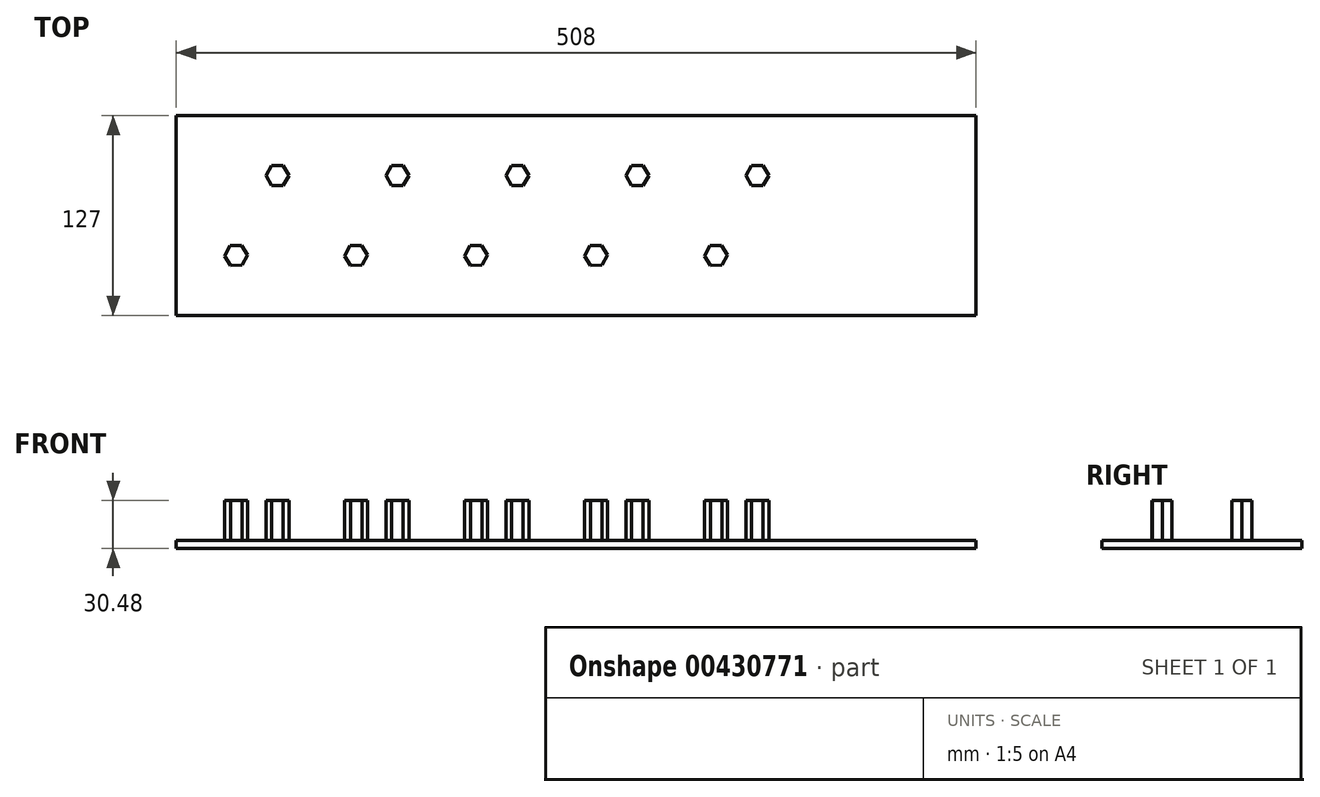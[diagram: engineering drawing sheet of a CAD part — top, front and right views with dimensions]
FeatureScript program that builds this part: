
annotation { "Feature Type Name" : "Feature", "Feature Type Description" : "" }
export const myFeature = defineFeature(function(context is Context, id is Id, definition is map)
    precondition{}
    {
        {
            var Q0;
            Q0=qCreatedBy(makeId("Top.planeOp"),FACE);
            var sketch = newSketch(context, id + "F0", { "sketchPlane" : qUnion([Q0])});
            skLineSegment(sketch, "E0.bottom", {"start": v(0, 0) * mm, "end": v(508, 0) * mm});
            skLineSegment(sketch, "E0.top", {"start": v(0, 127) * mm, "end": v(508, 127) * mm});
            skLineSegment(sketch, "E0.left", {"start": v(0, 0) * mm, "end": v(0, 127) * mm});
            skLineSegment(sketch, "E0.right", {"start": v(508, 0) * mm, "end": v(508, 127) * mm});
            skSolve(sketch);
        }
        {
            var Q0;
            Q0=makeQuery(id+"F0.imprint","IMPRINT",FACE,{"disambiguationData":[TD([[makeQuery(id+"F0.imprint","IMPRINT",EDGE,{"derivedFrom":sQuery(id+"F0.wireOp",EDGE,"E0.bottom")}),1.0]])]});
            extrude(context, id + "F1", {"entities" : qUnion([Q0]), "depth" : 5.08 * mm});
        }
        {
            var Q0;
            Q0=makeQuery(id+"F1.opExtrude","CAP_FACE",FACE,{"disambiguationData":[OSD([sQuery(id+"F0.wireOp",EDGE,"E0.bottom"),sQuery(id+"F0.wireOp",EDGE,"E0.top"),sQuery(id+"F0.wireOp",EDGE,"E0.left"),sQuery(id+"F0.wireOp",EDGE,"E0.right")])],"isStart":false});
            var sketch = newSketch(context, id + "F2", { "sketchPlane" : qUnion([Q0])});
            skCircle(sketch, "E1.cCircle", {"center": v(38.1, 38.1) * mm, "radius": 6.29 * mm, "construction": true});
            skLineSegment(sketch, "E1.0", {"start": v(41.55, 44.49) * mm, "end": v(45.36, 38.3) * mm});
            skLineSegment(sketch, "E1.1", {"start": v(45.36, 38.3) * mm, "end": v(41.9, 31.92) * mm});
            skLineSegment(sketch, "E1.2", {"start": v(41.9, 31.92) * mm, "end": v(34.65, 31.71) * mm});
            skLineSegment(sketch, "E1.3", {"start": v(34.65, 31.71) * mm, "end": v(30.84, 37.9) * mm});
            skLineSegment(sketch, "E1.4", {"start": v(30.84, 37.9) * mm, "end": v(34.3, 44.28) * mm});
            skLineSegment(sketch, "E1.5", {"start": v(34.3, 44.28) * mm, "end": v(41.55, 44.49) * mm});
            skPoint(sketch, "E1.0.midPoint", {"position": v(43.45, 41.4) * mm});
            skCircle(sketch, "E2.cCircle", {"center": v(64.28, 88.9) * mm, "radius": 6.29 * mm, "construction": true});
            skLineSegment(sketch, "E2.0", {"start": v(71.54, 88.9) * mm, "end": v(67.9, 82.6) * mm});
            skLineSegment(sketch, "E2.1", {"start": v(67.9, 82.6) * mm, "end": v(60.64, 82.62) * mm});
            skLineSegment(sketch, "E2.2", {"start": v(60.64, 82.62) * mm, "end": v(57.02, 88.9) * mm});
            skLineSegment(sketch, "E2.3", {"start": v(57.02, 88.9) * mm, "end": v(60.66, 95.2) * mm});
            skLineSegment(sketch, "E2.4", {"start": v(60.66, 95.2) * mm, "end": v(67.92, 95.18) * mm});
            skLineSegment(sketch, "E2.5", {"start": v(67.92, 95.18) * mm, "end": v(71.54, 88.9) * mm});
            skPoint(sketch, "E2.0.midPoint", {"position": v(69.72, 85.75) * mm});
            skLineSegment(sketch, "E3.1.0.0", {"start": v(136.86, 95.2) * mm, "end": v(144.12, 95.18) * mm});
            skLineSegment(sketch, "E3.1.0.1", {"start": v(133.22, 88.9) * mm, "end": v(136.86, 95.2) * mm});
            skLineSegment(sketch, "E3.1.0.2", {"start": v(136.84, 82.62) * mm, "end": v(133.22, 88.9) * mm});
            skLineSegment(sketch, "E3.1.0.3", {"start": v(144.1, 82.6) * mm, "end": v(136.84, 82.62) * mm});
            skLineSegment(sketch, "E3.1.0.4", {"start": v(147.74, 88.9) * mm, "end": v(144.1, 82.6) * mm});
            skLineSegment(sketch, "E3.1.0.5", {"start": v(144.12, 95.18) * mm, "end": v(147.74, 88.9) * mm});
            skLineSegment(sketch, "E3.1.0.6", {"start": v(118.1, 31.92) * mm, "end": v(110.85, 31.71) * mm});
            skLineSegment(sketch, "E3.1.0.7", {"start": v(121.56, 38.3) * mm, "end": v(118.1, 31.92) * mm});
            skLineSegment(sketch, "E3.1.0.8", {"start": v(117.75, 44.49) * mm, "end": v(121.56, 38.3) * mm});
            skLineSegment(sketch, "E3.1.0.9", {"start": v(110.5, 44.28) * mm, "end": v(117.75, 44.49) * mm});
            skLineSegment(sketch, "E3.1.0.10", {"start": v(107.04, 37.9) * mm, "end": v(110.5, 44.28) * mm});
            skLineSegment(sketch, "E3.1.0.11", {"start": v(110.85, 31.71) * mm, "end": v(107.04, 37.9) * mm});
            skLineSegment(sketch, "E3.2.0.0", {"start": v(213.06, 95.2) * mm, "end": v(220.32, 95.18) * mm});
            skLineSegment(sketch, "E3.2.0.1", {"start": v(209.42, 88.9) * mm, "end": v(213.06, 95.2) * mm});
            skLineSegment(sketch, "E3.2.0.2", {"start": v(213.04, 82.62) * mm, "end": v(209.42, 88.9) * mm});
            skLineSegment(sketch, "E3.2.0.3", {"start": v(220.3, 82.6) * mm, "end": v(213.04, 82.62) * mm});
            skLineSegment(sketch, "E3.2.0.4", {"start": v(223.94, 88.9) * mm, "end": v(220.3, 82.6) * mm});
            skLineSegment(sketch, "E3.2.0.5", {"start": v(220.32, 95.18) * mm, "end": v(223.94, 88.9) * mm});
            skLineSegment(sketch, "E3.2.0.6", {"start": v(194.3, 31.92) * mm, "end": v(187.05, 31.71) * mm});
            skLineSegment(sketch, "E3.2.0.7", {"start": v(197.76, 38.3) * mm, "end": v(194.3, 31.92) * mm});
            skLineSegment(sketch, "E3.2.0.8", {"start": v(193.95, 44.49) * mm, "end": v(197.76, 38.3) * mm});
            skLineSegment(sketch, "E3.2.0.9", {"start": v(186.7, 44.28) * mm, "end": v(193.95, 44.49) * mm});
            skLineSegment(sketch, "E3.2.0.10", {"start": v(183.24, 37.9) * mm, "end": v(186.7, 44.28) * mm});
            skLineSegment(sketch, "E3.2.0.11", {"start": v(187.05, 31.71) * mm, "end": v(183.24, 37.9) * mm});
            skLineSegment(sketch, "E3.3.0.0", {"start": v(289.26, 95.2) * mm, "end": v(296.52, 95.18) * mm});
            skLineSegment(sketch, "E3.3.0.1", {"start": v(285.62, 88.9) * mm, "end": v(289.26, 95.2) * mm});
            skLineSegment(sketch, "E3.3.0.2", {"start": v(289.24, 82.62) * mm, "end": v(285.62, 88.9) * mm});
            skLineSegment(sketch, "E3.3.0.3", {"start": v(296.5, 82.6) * mm, "end": v(289.24, 82.62) * mm});
            skLineSegment(sketch, "E3.3.0.4", {"start": v(300.14, 88.9) * mm, "end": v(296.5, 82.6) * mm});
            skLineSegment(sketch, "E3.3.0.5", {"start": v(296.52, 95.18) * mm, "end": v(300.14, 88.9) * mm});
            skLineSegment(sketch, "E3.3.0.6", {"start": v(270.5, 31.92) * mm, "end": v(263.25, 31.71) * mm});
            skLineSegment(sketch, "E3.3.0.7", {"start": v(273.96, 38.3) * mm, "end": v(270.5, 31.92) * mm});
            skLineSegment(sketch, "E3.3.0.8", {"start": v(270.15, 44.49) * mm, "end": v(273.96, 38.3) * mm});
            skLineSegment(sketch, "E3.3.0.9", {"start": v(262.9, 44.28) * mm, "end": v(270.15, 44.49) * mm});
            skLineSegment(sketch, "E3.3.0.10", {"start": v(259.44, 37.9) * mm, "end": v(262.9, 44.28) * mm});
            skLineSegment(sketch, "E3.3.0.11", {"start": v(263.25, 31.71) * mm, "end": v(259.44, 37.9) * mm});
            skLineSegment(sketch, "E3.4.0.0", {"start": v(365.46, 95.2) * mm, "end": v(372.72, 95.18) * mm});
            skLineSegment(sketch, "E3.4.0.1", {"start": v(361.82, 88.9) * mm, "end": v(365.46, 95.2) * mm});
            skLineSegment(sketch, "E3.4.0.2", {"start": v(365.44, 82.62) * mm, "end": v(361.82, 88.9) * mm});
            skLineSegment(sketch, "E3.4.0.3", {"start": v(372.7, 82.6) * mm, "end": v(365.44, 82.62) * mm});
            skLineSegment(sketch, "E3.4.0.4", {"start": v(376.34, 88.9) * mm, "end": v(372.7, 82.6) * mm});
            skLineSegment(sketch, "E3.4.0.5", {"start": v(372.72, 95.18) * mm, "end": v(376.34, 88.9) * mm});
            skLineSegment(sketch, "E3.4.0.6", {"start": v(346.7, 31.92) * mm, "end": v(339.45, 31.71) * mm});
            skLineSegment(sketch, "E3.4.0.7", {"start": v(350.16, 38.3) * mm, "end": v(346.7, 31.92) * mm});
            skLineSegment(sketch, "E3.4.0.8", {"start": v(346.35, 44.49) * mm, "end": v(350.16, 38.3) * mm});
            skLineSegment(sketch, "E3.4.0.9", {"start": v(339.1, 44.28) * mm, "end": v(346.35, 44.49) * mm});
            skLineSegment(sketch, "E3.4.0.10", {"start": v(335.64, 37.9) * mm, "end": v(339.1, 44.28) * mm});
            skLineSegment(sketch, "E3.4.0.11", {"start": v(339.45, 31.71) * mm, "end": v(335.64, 37.9) * mm});
            skLineSegment(sketch, "E3.direction1", {"start": v(60.66, 95.2) * mm, "end": v(136.86, 95.2) * mm, "construction": true});
            skSolve(sketch);
        }
        {
            var Q0;
            Q0 = qSketchRegion(id + "F2", true);
            extrude(context, id + "F3", {"entities" : qUnion([Q0]), "operationType" : NewBodyOperationType.ADD, "depth" : 25.4 * mm});
        }
    });
